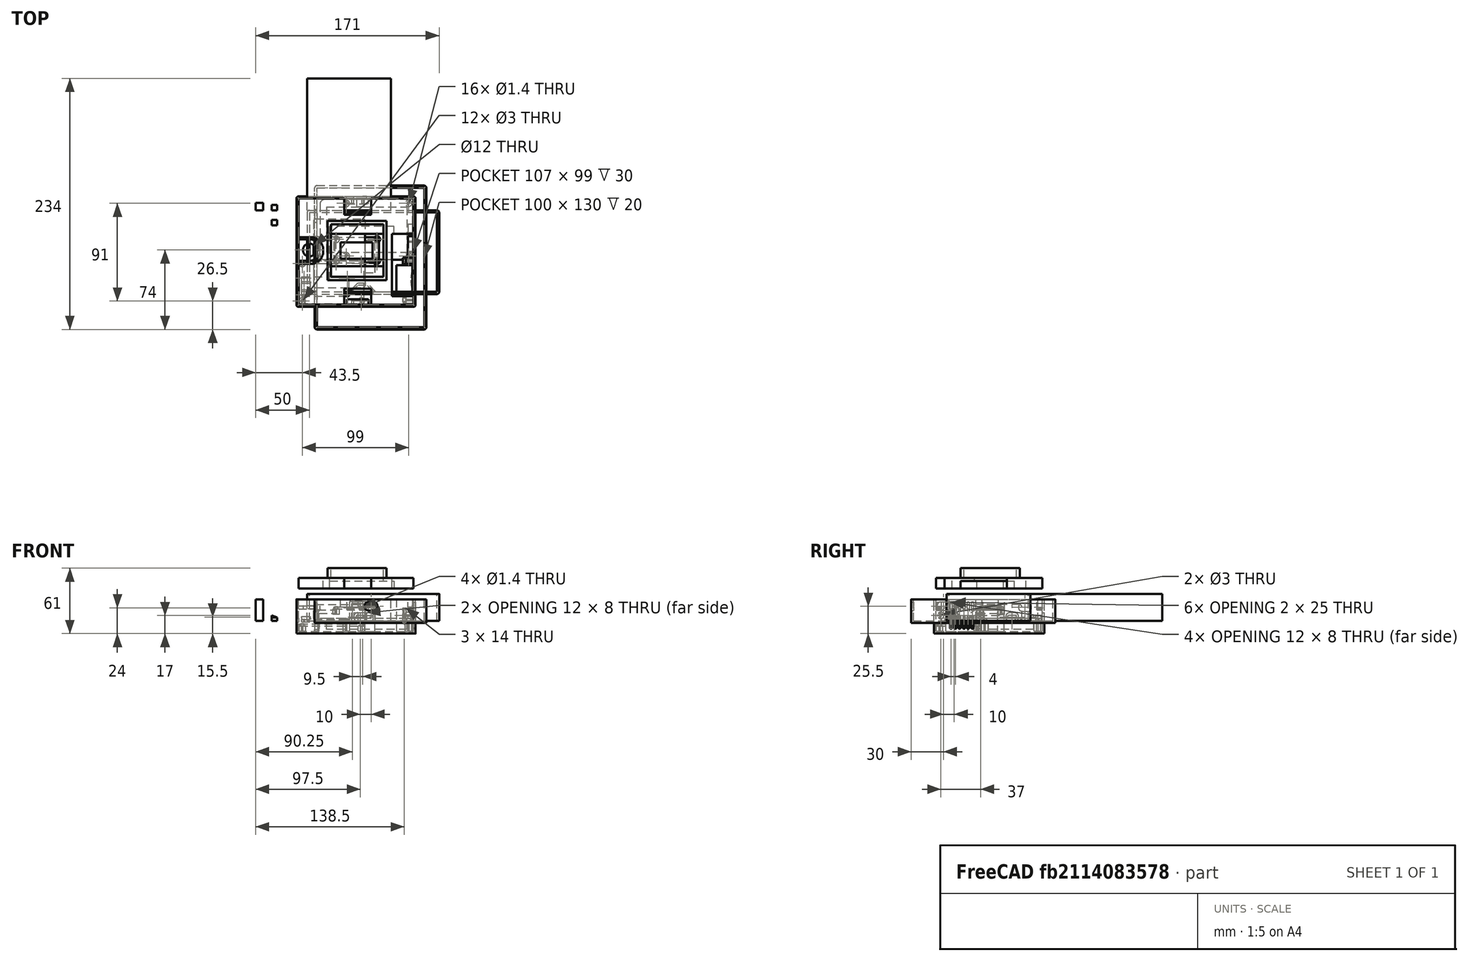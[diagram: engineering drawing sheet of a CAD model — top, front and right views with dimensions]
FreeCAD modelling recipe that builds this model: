
FCSTD DOCUMENT  (FreeCAD 1.0R39109 (Git))
Label: kitchen_timer
License: All rights reserved
LicenseURL: http://en.wikipedia.org/wiki/All_rights_reserved
objects: Part::Box×55, Part::Cut×34, Part::Cylinder×27, Part::Fillet×23, Part::MultiFuse×21, Part::FeaturePython×14, Part::Chamfer×4, Part::Sphere×1
note: 179 computed .brp shape members not serialized (recipe doc carries the construction recipe); baked Part::Feature solids carry a one-line shape summary decoded from their .brp

FEATURE [Part::Box] Box  label="Cube"
  AttacherType = Attacher::AttachEngine3D
  Height = 25
  Length = 78
  Width = 123
FEATURE [Part::Box] Box001  label="Cube001"
  AttacherType = Attacher::AttachEngine3D
  Height = 15
  Length = 64
  Placement = pos=(6,-8,0) rot=(0,0,1;-1.5708rad)
  Width = 48
FEATURE [Part::Box] Box002  label="Cube002"
  AttacherType = Attacher::AttachEngine3D
  Height = 25
  Length = 74
  Placement = pos=(2,2,0) rot=(0,0,1;0rad)
  Width = 119
FEATURE [Part::Box] Box003  label="Cube003"
  AttacherType = Attacher::AttachEngine3D
  Height = 25
  Length = 78
  Width = 123
FEATURE [Part::Fillet] Fillet
  Base = -> Box
  EdgeLinks = -> Box [Edge1,Edge3,Edge5]
  Edges = 3 edges r=2: [Edge1,Edge3,Edge5]
FEATURE [Part::Cut] Cut  label="case"
  Base = -> Fillet
  Placement = pos=(0,0,0) rot=(0,0,1;-1.5708rad)
  Tool = -> Box002
FEATURE [Part::Fillet] Fillet001  label="Battery pack_1"
  Base = -> Box001
  EdgeLinks = -> Box001 [Edge1,Edge2,Edge3,Edge4,Edge5,Edge6,Edge7,Edge8,Edge9,Edge10,Edge11,Edge12]
  Edges = 12 edges r=2: [Edge1,Edge2,Edge3,Edge4,Edge5,Edge6,Edge7,Edge8,Edge9,Edge10,Edge11,Edge12]
FEATURE [Part::Box] Box004  label="Cube004"
  AttacherType = Attacher::AttachEngine3D
  Height = 7
  Length = 30
  Placement = pos=(0,0,2) rot=(0,0,1;0rad)
  Width = 15
FEATURE [Part::Box] Box005  label="Cube005"
  AttacherType = Attacher::AttachEngine3D
  Height = 2
  Length = 42
  Placement = pos=(-6,-4,0) rot=(0,0,1;0rad)
  Width = 24
FEATURE [Part::MultiFuse] Fusion
  Shapes = -> [Box004,Box005]
FEATURE [Part::Cylinder] Cylinder
  Angle = 360
  AttacherType = Attacher::AttachEngine3D
  FirstAngle = 0
  Height = 10
  Placement = pos=(0,0,-2) rot=(0,0,1;0rad)
  Radius = 1.5
  SecondAngle = 0
FEATURE [Part::Cylinder] Cylinder001
  Angle = 360
  AttacherType = Attacher::AttachEngine3D
  FirstAngle = 0
  Height = 10
  Placement = pos=(38,0,-2) rot=(0,0,1;0rad)
  Radius = 1.5
  SecondAngle = 0
FEATURE [Part::Cylinder] Cylinder002
  Angle = 360
  AttacherType = Attacher::AttachEngine3D
  FirstAngle = 0
  Height = 10
  Placement = pos=(38,20,-2) rot=(0,0,1;0rad)
  Radius = 1.5
  SecondAngle = 0
FEATURE [Part::Cylinder] Cylinder003
  Angle = 360
  AttacherType = Attacher::AttachEngine3D
  FirstAngle = 0
  Height = 10
  Placement = pos=(0,20,-2) rot=(0,0,1;0rad)
  Radius = 1.5
  SecondAngle = 0
FEATURE [Part::MultiFuse] Fusion001
  Placement = pos=(-4,-2,0) rot=(0,0,1;0rad)
  Shapes = -> [Cylinder003,Cylinder,Cylinder001,Cylinder002]
FEATURE [Part::Cut] Cut001  label="display"
  Base = -> Fusion
  Placement = pos=(31,-45,11) rot=(0,0,1;0rad)
  Tool = -> Fusion001
FEATURE [Part::Box] Box006  label="Cube006"
  AttacherType = Attacher::AttachEngine3D
  Height = 15
  Length = 30
  Width = 28
FEATURE [Part::Sphere] Sphere
  Angle1 = -90
  Angle2 = 90
  Angle3 = 360
  AttacherType = Attacher::AttachEngine3D
  Placement = pos=(15,14,43.5) rot=(0,0,1;0rad)
  Radius = 30
FEATURE [Part::Cut] Cut002
  Base = -> Box006
  Tool = -> Sphere
FEATURE [Part::Box] Box007  label="Cube007"
  AttacherType = Attacher::AttachEngine3D
  Height = 3
  Length = 14
  Placement = pos=(8,27,6) rot=(0,0,1;0rad)
  Width = 8
FEATURE [Part::Chamfer] Chamfer
  Base = -> Box007
  EdgeLinks = -> Box007 [Edge3,Edge7]
  Edges = 2 edges r=6: [Edge3,Edge7]
FEATURE [Part::Cylinder] Cylinder004
  Angle = 360
  AttacherType = Attacher::AttachEngine3D
  FirstAngle = 0
  Height = 10
  Placement = pos=(15,32.5,0) rot=(0,0,1;0rad)
  Radius = 1.5
  SecondAngle = 0
FEATURE [Part::Cut] Cut003
  Base = -> Chamfer
  Tool = -> Cylinder004
FEATURE [Part::Box] Box008  label="Cube008"
  AttacherType = Attacher::AttachEngine3D
  Height = 3
  Length = 14
  Placement = pos=(8,27,6) rot=(0,0,1;0rad)
  Width = 8
FEATURE [Part::Chamfer] Chamfer001
  Base = -> Box008
  EdgeLinks = -> Box008 [Edge3,Edge7]
  Edges = 2 edges r=6: [Edge3,Edge7]
FEATURE [Part::Cylinder] Cylinder005
  Angle = 360
  AttacherType = Attacher::AttachEngine3D
  FirstAngle = 0
  Height = 10
  Placement = pos=(15,32.5,0) rot=(0,0,1;0rad)
  Radius = 1.5
  SecondAngle = 0
FEATURE [Part::Cut] Cut004
  Base = -> Chamfer001
  Placement = pos=(30,28,0) rot=(0,0,1;3.14159rad)
  Tool = -> Cylinder005
FEATURE [Part::MultiFuse] Fusion002  label="speaker"
  Placement = pos=(83,-79,20) rot=(0,1,0;1.5708rad)
  Shapes = -> [Cut003,Cut002,Cut004]
FEATURE [Part::Fillet] Fillet002  label="case001"
  Base = -> Cut
  EdgeLinks = -> Cut [Edge28]
  Edges = 1 edges r=2: [Edge28]
FEATURE [Part::Box] Box009  label="Cube009"
  AttacherType = Attacher::AttachEngine3D
  Height = 2
  Length = 44
  Width = 18
FEATURE [Part::Box] Box010  label="Cube010"
  AttacherType = Attacher::AttachEngine3D
  Height = 3
  Length = 8
  Placement = pos=(0,0,2) rot=(0,0,1;0rad)
  Width = 9
FEATURE [Part::Fillet] Fillet003
  Base = -> Box010
  EdgeLinks = -> Box010 [Edge9,Edge10,Edge11,Edge12]
  Edges = 4 edges r=1.4: [Edge9,Edge10,Edge11,Edge12]
  Placement = pos=(0,4.5,0) rot=(0,0,1;0rad)
FEATURE [Part::MultiFuse] Fusion003  label="nano"
  Placement = pos=(17,-22,14) rot=(0,0,1;0rad)
  Shapes = -> [Fillet003,Box009]
FEATURE [Part::Box] Box011  label="Cube011"
  AttacherType = Attacher::AttachEngine3D
  Height = 2
  Length = 86
  Placement = pos=(0,0,10) rot=(0,0,1;0rad)
  Width = 56
FEATURE [Part::Box] Box012  label="Cube012"
  AttacherType = Attacher::AttachEngine3D
  Height = 10
  Length = 75
  Placement = pos=(5,7,2) rot=(0,0,1;0rad)
  Width = 42
FEATURE [Part::Cylinder] Cylinder006
  Angle = 360
  AttacherType = Attacher::AttachEngine3D
  FirstAngle = 0
  Height = 10
  Radius = 1.5
  SecondAngle = 0
FEATURE [Part::Cylinder] Cylinder007
  Angle = 360
  AttacherType = Attacher::AttachEngine3D
  FirstAngle = 0
  Height = 10
  Placement = pos=(58,0,0) rot=(0,0,1;0rad)
  Radius = 1.5
  SecondAngle = 0
FEATURE [Part::Cylinder] Cylinder008
  Angle = 360
  AttacherType = Attacher::AttachEngine3D
  FirstAngle = 0
  Height = 10
  Placement = pos=(0,49,0) rot=(0,0,1;0rad)
  Radius = 1.5
  SecondAngle = 0
FEATURE [Part::Cylinder] Cylinder009
  Angle = 360
  AttacherType = Attacher::AttachEngine3D
  FirstAngle = 0
  Height = 10
  Placement = pos=(58,49,0) rot=(0,0,1;0rad)
  Radius = 1.5
  SecondAngle = 0
FEATURE [Part::MultiFuse] Fusion004
  Placement = pos=(6.5,-63.5,4) rot=(0,0,1;0rad)
  Shapes = -> [Cylinder006,Cylinder007,Cylinder008,Cylinder009]
FEATURE [Part::MultiFuse] Fusion005
  Placement = pos=(0,-67,0) rot=(0,0,1;0rad)
  Shapes = -> [Box011,Box012]
FEATURE [Part::Box] Box013  label="Cube013"
  AttacherType = Attacher::AttachEngine3D
  Height = 3
  Length = 7
  Placement = pos=(45,-67,12) rot=(0,0,1;0rad)
  Width = 7
FEATURE [Part::MultiFuse] Fusion006
  Placement = pos=(3,0,0) rot=(0,0,1;0rad)
  Shapes = -> [Fusion005,Box013]
FEATURE [Part::Cut] Cut005
  Base = -> Fusion006
  Tool = -> Fusion004
FEATURE [Part::Fillet] Fillet004  label="power_pack"
  Base = -> Cut005
  EdgeLinks = -> Cut005 [Edge28,Edge29,Edge31,Edge32]
  Edges = 4 edges r=4: [Edge28,Edge29,Edge31,Edge32]
  Placement = pos=(8,-41,0) rot=(0,0,1;0rad)
FEATURE [Part::Box] Box014  label="Cube014"
  AttacherType = Attacher::AttachEngine3D
  Height = 18
  Length = 20
  Placement = pos=(41.5,-76.5,0) rot=(0,0,1;0rad)
  Width = 9
FEATURE [Part::Chamfer] Chamfer002
  Base = -> Box014
  EdgeLinks = -> Box014 [Edge3,Edge7]
  Edges = 2 edges r=6: [Edge3,Edge7]
  Placement = pos=(0,-2,-2) rot=(0,0,1;0rad)
FEATURE [Part::Box] Box015  label="Cube015"
  AttacherType = Attacher::AttachEngine3D
  Height = 18
  Length = 24
  Placement = pos=(39.5,-76.5,0) rot=(0,0,1;0rad)
  Width = 9
FEATURE [Part::Chamfer] Chamfer003
  Base = -> Box015
  EdgeLinks = -> Box015 [Edge3,Edge7]
  Edges = 2 edges r=8: [Edge3,Edge7]
FEATURE [Part::MultiFuse] Fusion007
  Shapes = -> [Fillet002,Chamfer003]
FEATURE [Part::Cut] Cut006
  Base = -> Fusion007
  Tool = -> Chamfer002
FEATURE [Part::Cylinder] Cylinder010
  Angle = 360
  AttacherType = Attacher::AttachEngine3D
  FirstAngle = 0
  Height = 10
  Radius = 0.7
  SecondAngle = 0
FEATURE [Part::Cylinder] Cylinder011
  Angle = 360
  AttacherType = Attacher::AttachEngine3D
  FirstAngle = 0
  Height = 10
  Placement = pos=(40.5,0,0) rot=(0,0,1;0rad)
  Radius = 0.7
  SecondAngle = 0
FEATURE [Part::Cylinder] Cylinder012
  Angle = 360
  AttacherType = Attacher::AttachEngine3D
  FirstAngle = 0
  Height = 10
  Placement = pos=(0,15.5,0) rot=(0,0,1;0rad)
  Radius = 0.7
  SecondAngle = 0
FEATURE [Part::Cylinder] Cylinder013
  Angle = 360
  AttacherType = Attacher::AttachEngine3D
  FirstAngle = 0
  Height = 10
  Placement = pos=(40.5,15.5,0) rot=(0,0,1;0rad)
  Radius = 0.7
  SecondAngle = 0
FEATURE [Part::MultiFuse] Fusion008
  Placement = pos=(19,-20.75,7) rot=(0,0,1;0rad)
  Shapes = -> [Cylinder010,Cylinder011,Cylinder012,Cylinder013]
FEATURE [Part::Cut] Cut007  label="nano001"
  Base = -> Fusion003
  Placement = pos=(-15,29,-7) rot=(0,0,1;0rad)
  Tool = -> Fusion008
FEATURE [Part::Box] Box016  label="Cube016"
  AttacherType = Attacher::AttachEngine3D
  Height = 3
  Length = 4
  Placement = pos=(11,-85,12) rot=(0,0,1;0rad)
  Width = 8
FEATURE [Part::MultiFuse] Fusion009  label="power_pack001"
  Placement = pos=(109,-98,-10) rot=(0,0,1;3.14159rad)
  Shapes = -> [Fillet004,Box016]
FEATURE [Part::Box] Box017  label="Cube017"
  AttacherType = Attacher::AttachEngine3D
  Height = 2
  Length = 60
  Placement = pos=(0,0,3) rot=(0,0,1;0rad)
  Width = 40
FEATURE [Part::Cylinder] Cylinder014
  Angle = 360
  AttacherType = Attacher::AttachEngine3D
  FirstAngle = 0
  Height = 10
  Radius = 1.5
  SecondAngle = 0
FEATURE [Part::Cylinder] Cylinder015
  Angle = 360
  AttacherType = Attacher::AttachEngine3D
  FirstAngle = 0
  Height = 10
  Placement = pos=(55,0,0) rot=(0,0,1;0rad)
  Radius = 1.5
  SecondAngle = 0
FEATURE [Part::Cylinder] Cylinder016
  Angle = 360
  AttacherType = Attacher::AttachEngine3D
  FirstAngle = 0
  Height = 10
  Placement = pos=(0,35,0) rot=(0,0,1;0rad)
  Radius = 1.5
  SecondAngle = 0
FEATURE [Part::Cylinder] Cylinder017
  Angle = 360
  AttacherType = Attacher::AttachEngine3D
  FirstAngle = 0
  Height = 10
  Placement = pos=(55,35,0) rot=(0,0,1;0rad)
  Radius = 1.5
  SecondAngle = 0
FEATURE [Part::MultiFuse] Fusion010
  Placement = pos=(2.5,2.5,0) rot=(0,0,1;0rad)
  Shapes = -> [Cylinder014,Cylinder015,Cylinder016,Cylinder017]
FEATURE [Part::Cut] Cut008  label="board_1"
  Base = -> Box017
  Tool = -> Fusion010
FEATURE [Part::MultiFuse] Fusion011  label="nano_and_board"
  Placement = pos=(-7,-87,-8) rot=(0,0,1;0rad)
  Shapes = -> [Cut007,Cut008]
FEATURE [Part::FeaturePython] Tube  # WARN: FeaturePython — macro-defined, semantics opaque (R4)
  AttacherType = Attacher::AttachEngine3D
  Height = 5
  InnerRadius = 0.7
  OuterRadius = 3
  Placement = pos=(12.5,-18.5,0) rot=(0,0,1;0rad)
FEATURE [Part::FeaturePython] Tube001  # WARN: FeaturePython — macro-defined, semantics opaque (R4)
  AttacherType = Attacher::AttachEngine3D
  Height = 5
  InnerRadius = 0.7
  OuterRadius = 3
  Placement = pos=(67.5,-18.5,0) rot=(0,0,1;0rad)
FEATURE [Part::FeaturePython] Tube002  # WARN: FeaturePython — macro-defined, semantics opaque (R4)
  AttacherType = Attacher::AttachEngine3D
  Height = 5
  InnerRadius = 0.7
  OuterRadius = 3
  Placement = pos=(12.5,16.5,0) rot=(0,0,1;0rad)
FEATURE [Part::FeaturePython] Tube003  # WARN: FeaturePython — macro-defined, semantics opaque (R4)
  AttacherType = Attacher::AttachEngine3D
  Height = 5
  InnerRadius = 0.7
  OuterRadius = 3
  Placement = pos=(67.5,16.5,0) rot=(0,0,1;0rad)
FEATURE [Part::FeaturePython] Tube004  # WARN: FeaturePython — macro-defined, semantics opaque (R4)
  AttacherType = Attacher::AttachEngine3D
  Height = 7
  InnerRadius = 0.7
  OuterRadius = 3
  Placement = pos=(92,-9.5,0) rot=(0,0,1;0rad)
FEATURE [Part::FeaturePython] Tube005  # WARN: FeaturePython — macro-defined, semantics opaque (R4)
  AttacherType = Attacher::AttachEngine3D
  Height = 7
  InnerRadius = 0.7
  OuterRadius = 3
  Placement = pos=(92,-46.5,0) rot=(0,0,1;0rad)
FEATURE [Part::FeaturePython] Tube006  # WARN: FeaturePython — macro-defined, semantics opaque (R4)
  AttacherType = Attacher::AttachEngine3D
  Height = 5
  InnerRadius = 0.7
  OuterRadius = 3
  Placement = pos=(65,-47,0) rot=(0,0,1;0rad)
FEATURE [Part::FeaturePython] Tube007  # WARN: FeaturePython — macro-defined, semantics opaque (R4)
  AttacherType = Attacher::AttachEngine3D
  Height = 5
  InnerRadius = 0.7
  OuterRadius = 3
  Placement = pos=(65,-27,0) rot=(0,0,1;0rad)
FEATURE [Part::FeaturePython] Tube008  # WARN: FeaturePython — macro-defined, semantics opaque (R4)
  AttacherType = Attacher::AttachEngine3D
  Height = 5
  InnerRadius = 0.7
  OuterRadius = 3
  Placement = pos=(27,-27,0) rot=(0,0,1;0rad)
FEATURE [Part::FeaturePython] Tube009  # WARN: FeaturePython — macro-defined, semantics opaque (R4)
  AttacherType = Attacher::AttachEngine3D
  Height = 10
  InnerRadius = 0.7
  OuterRadius = 3
  Placement = pos=(14.5,-104.5,0) rot=(0,0,1;0rad)
FEATURE [Part::FeaturePython] Tube010  # WARN: FeaturePython — macro-defined, semantics opaque (R4)
  AttacherType = Attacher::AttachEngine3D
  Height = 5
  InnerRadius = 0.7
  OuterRadius = 3
  Placement = pos=(27,-47,0) rot=(0,0,1;0rad)
FEATURE [Part::FeaturePython] Tube011  # WARN: FeaturePython — macro-defined, semantics opaque (R4)
  AttacherType = Attacher::AttachEngine3D
  Height = 10
  InnerRadius = 0.7
  OuterRadius = 3
  Placement = pos=(14.5,-55.5,0) rot=(0,0,1;0rad)
FEATURE [Part::FeaturePython] Tube012  # WARN: FeaturePython — macro-defined, semantics opaque (R4)
  AttacherType = Attacher::AttachEngine3D
  Height = 10
  InnerRadius = 0.7
  OuterRadius = 3
  Placement = pos=(72.5,-55.5,0) rot=(0,0,1;0rad)
FEATURE [Part::FeaturePython] Tube013  # WARN: FeaturePython — macro-defined, semantics opaque (R4)
  AttacherType = Attacher::AttachEngine3D
  Height = 10
  InnerRadius = 0.7
  OuterRadius = 3
  Placement = pos=(72.5,-104.5,0) rot=(0,0,1;0rad)
FEATURE [Part::Box] Box018  label="Cube018"
  AttacherType = Attacher::AttachEngine3D
  Height = 20
  Length = 100
  Placement = pos=(9,-109,0) rot=(0,0,1;0rad)
  Width = 130
FEATURE [Part::Box] Box019  label="Cube019"
  AttacherType = Attacher::AttachEngine3D
  Height = 22
  Length = 104
  Placement = pos=(7,-111,-2) rot=(0,0,1;0rad)
  Width = 134
FEATURE [Part::Cut] Cut009
  Base = -> Box019
  Tool = -> Box018
FEATURE [Part::Box] Box020  label="Cube020"
  AttacherType = Attacher::AttachEngine3D
  Height = 8
  Length = 10
  Placement = pos=(4,-3,0) rot=(0,0,1;0rad)
  Width = 12
FEATURE [Part::Fillet] Fillet005
  Base = -> Box020
  EdgeLinks = -> Box020 [Edge9,Edge10,Edge11,Edge12]
  Edges = 4 edges r=3.7: [Edge9,Edge10,Edge11,Edge12]
  Placement = pos=(0,-8,8.5) rot=(0,0,1;0rad)
FEATURE [Part::Box] Box021  label="Cube021"
  AttacherType = Attacher::AttachEngine3D
  Height = 8
  Length = 10
  Placement = pos=(4,-3,0) rot=(0,0,1;0rad)
  Width = 12
FEATURE [Part::Fillet] Fillet006
  Base = -> Box021
  EdgeLinks = -> Box021 [Edge9,Edge10,Edge11,Edge12]
  Edges = 4 edges r=3.7: [Edge9,Edge10,Edge11,Edge12]
  Placement = pos=(0,-84,9.5) rot=(0,0,1;0rad)
FEATURE [Part::Box] Box022  label="Cube022"
  AttacherType = Attacher::AttachEngine3D
  Height = 8
  Length = 10
  Placement = pos=(4,-3,0) rot=(0,0,1;0rad)
  Width = 12
FEATURE [Part::Fillet] Fillet007
  Base = -> Box022
  EdgeLinks = -> Box022 [Edge9,Edge10,Edge11,Edge12]
  Edges = 4 edges r=3.7: [Edge9,Edge10,Edge11,Edge12]
  Placement = pos=(62.5,-118,9.5) rot=(0,0,1;1.5708rad)
FEATURE [Part::Cut] Cut010
  Base = -> Cut009
  Tool = -> Fillet005
FEATURE [Part::Cut] Cut011
  Base = -> Cut010
  Tool = -> Fillet007
FEATURE [Part::Cut] Cut012
  Base = -> Cut011
  Tool = -> Fillet006
FEATURE [Part::Fillet] Fillet008
  Base = -> Cut012
  EdgeLinks = -> Cut012 [Edge1,Edge4,Edge22,Edge40]
  Edges = 4 edges r=2: [Edge1,Edge4,Edge22,Edge40]
FEATURE [Part::Box] Box023  label="Cube023"
  AttacherType = Attacher::AttachEngine3D
  Height = 10
  Length = 20
  Placement = pos=(57,16,10) rot=(0,0,1;0rad)
  Width = 5
FEATURE [Part::Cylinder] Cylinder018
  Angle = 360
  AttacherType = Attacher::AttachEngine3D
  FirstAngle = 0
  Height = 10
  Placement = pos=(71.75,22,17) rot=(1,0,0;1.5708rad)
  Radius = 0.7
  SecondAngle = 0
FEATURE [Part::Cylinder] Cylinder019
  Angle = 360
  AttacherType = Attacher::AttachEngine3D
  FirstAngle = 0
  Height = 10
  Placement = pos=(62.25,22,17) rot=(1,0,0;1.5708rad)
  Radius = 0.7
  SecondAngle = 0
FEATURE [Part::MultiFuse] Fusion013
  Placement = pos=(0,0,-5) rot=(0,0,1;0rad)
  Shapes = -> [Cylinder019,Cylinder018]
FEATURE [Part::Cut] Cut013  label="up_button_stand"
  Base = -> Box023
  Placement = pos=(-20,-10,0) rot=(0,0,1;0rad)
  Tool = -> Fusion013
FEATURE [Part::Box] Box024  label="Cube024"
  AttacherType = Attacher::AttachEngine3D
  Height = 10
  Length = 20
  Placement = pos=(57,16,10) rot=(0,0,1;0rad)
  Width = 5
FEATURE [Part::Cylinder] Cylinder020
  Angle = 360
  AttacherType = Attacher::AttachEngine3D
  FirstAngle = 0
  Height = 10
  Placement = pos=(71.75,22,17) rot=(1,0,0;1.5708rad)
  Radius = 0.7
  SecondAngle = 0
FEATURE [Part::Cylinder] Cylinder021
  Angle = 360
  AttacherType = Attacher::AttachEngine3D
  FirstAngle = 0
  Height = 10
  Placement = pos=(62.25,22,17) rot=(1,0,0;1.5708rad)
  Radius = 0.7
  SecondAngle = 0
FEATURE [Part::MultiFuse] Fusion014
  Placement = pos=(0,0,-5) rot=(0,0,1;0rad)
  Shapes = -> [Cylinder021,Cylinder020]
FEATURE [Part::Cut] Cut014  label="down_button_stand"
  Base = -> Box024
  Placement = pos=(-20,-104,0) rot=(0,0,1;0rad)
  Tool = -> Fusion014
FEATURE [Part::MultiFuse] Fusion015  label="boardstand"
  Placement = pos=(-17,-66,-10) rot=(0,0,1;0rad)
  Shapes = -> [Tube,Tube001,Tube002,Tube003]
FEATURE [Part::MultiFuse] Fusion016  label="spkrstand"
  Placement = pos=(92,-37,97) rot=(0,1,0;1.5708rad)
  Shapes = -> [Tube004,Tube005]
FEATURE [Part::MultiFuse] Fusion017  label="dsplystand"
  Placement = pos=(0,0,6) rot=(0,0,1;0rad)
  Shapes = -> [Tube006,Tube007,Tube008,Tube010]
FEATURE [Part::MultiFuse] Fusion018  label="powerstand"
  Placement = pos=(22,62,-10) rot=(0,0,1;0rad)
  Shapes = -> [Tube009,Tube011,Tube012,Tube013]
FEATURE [Part::Box] Box025  label="Cube025"
  AttacherType = Attacher::AttachEngine3D
  Height = 10
  Length = 20
  Placement = pos=(57,16,10) rot=(0,0,1;0rad)
  Width = 5
FEATURE [Part::Cylinder] Cylinder022
  Angle = 360
  AttacherType = Attacher::AttachEngine3D
  FirstAngle = 0
  Height = 10
  Placement = pos=(71.75,22,17) rot=(1,0,0;1.5708rad)
  Radius = 0.7
  SecondAngle = 0
FEATURE [Part::Cylinder] Cylinder023
  Angle = 360
  AttacherType = Attacher::AttachEngine3D
  FirstAngle = 0
  Height = 10
  Placement = pos=(62.25,22,17) rot=(1,0,0;1.5708rad)
  Radius = 0.7
  SecondAngle = 0
FEATURE [Part::MultiFuse] Fusion019
  Placement = pos=(0,0,-5) rot=(0,0,1;0rad)
  Shapes = -> [Cylinder023,Cylinder022]
FEATURE [Part::Cut] Cut015  label="right_button_stand"
  Base = -> Box025
  Placement = pos=(115,-101,0) rot=(0,0,1;1.5708rad)
  Tool = -> Fusion019
FEATURE [Part::Box] Box026  label="Cube026"
  AttacherType = Attacher::AttachEngine3D
  Height = 3
  Length = 20
  Placement = pos=(-10,-10,4) rot=(0,0,1;0rad)
  Width = 20
FEATURE [Part::Cylinder] Cylinder024
  Angle = 360
  AttacherType = Attacher::AttachEngine3D
  FirstAngle = 0
  Height = 10
  Radius = 6
  SecondAngle = 0
FEATURE [Part::Cut] Cut016
  Base = -> Box026
  Placement = pos=(2,-37,7) rot=(0,0,1;0rad)
  Tool = -> Cylinder024
FEATURE [Part::Box] Box027  label="Cube027"
  AttacherType = Attacher::AttachEngine3D
  Height = 32
  Length = 107
  Placement = pos=(-8,-88,-10) rot=(0,0,1;0rad)
  Width = 99
FEATURE [Part::Box] Box028  label="Cube028"
  AttacherType = Attacher::AttachEngine3D
  Height = 32
  Length = 111
  Placement = pos=(-10,-90,-12) rot=(0,0,1;0rad)
  Width = 103
FEATURE [Part::Cut] Cut017
  Base = -> Box028
  Tool = -> Box027
FEATURE [Part::Fillet] Fillet009
  Base = -> Cut016
  EdgeLinks = -> Cut016 [Edge6,Edge12]
  Edges = 2 edges r=9.7: [Edge6,Edge12]
FEATURE [Part::Box] Box029  label="Cube029"
  AttacherType = Attacher::AttachEngine3D
  Height = 20
  Length = 19
  Placement = pos=(7,0,-10) rot=(0,0,1;0rad)
  Width = 25
FEATURE [Part::Box] Box030  label="Cube030"
  AttacherType = Attacher::AttachEngine3D
  Height = 20
  Length = 19
  Placement = pos=(11,0,-13) rot=(0,0,1;0rad)
  Width = 25
FEATURE [Part::Cut] Cut018
  Base = -> Box029
  Placement = pos=(0,-49.5,0) rot=(0,0,1;0rad)
  Tool = -> Box030
FEATURE [Part::Cylinder] Cylinder025
  Angle = 360
  AttacherType = Attacher::AttachEngine3D
  FirstAngle = 0
  Height = 30
  Placement = pos=(2,-37,-13) rot=(0,0,1;0rad)
  Radius = 8
  SecondAngle = 0
FEATURE [Part::Cut] Cut019
  Base = -> Cut018
  Tool = -> Cylinder025
FEATURE [Part::Cylinder] Cylinder026
  Angle = 360
  AttacherType = Attacher::AttachEngine3D
  FirstAngle = 0
  Height = 10
  Placement = pos=(2,-49.5,-4) rot=(0,1,0;1.5708rad)
  Radius = 4
  SecondAngle = 0
FEATURE [Part::Cut] Cut020
  Base = -> Cut019
  Tool = -> Cylinder026
FEATURE [Part::Box] Box031  label="Cube031"
  AttacherType = Attacher::AttachEngine3D
  Height = 20
  Length = 9
  Placement = pos=(54,-58,-10) rot=(0,0,1;0rad)
  Width = 30
FEATURE [Part::Box] Box032  label="Cube032"
  AttacherType = Attacher::AttachEngine3D
  Height = 15
  Length = 9
  Placement = pos=(54,-48,-10) rot=(0,0,1;0rad)
  Width = 20
FEATURE [Part::Cut] Cut021
  Base = -> Box031
  Tool = -> Box032
FEATURE [Part::Fillet] Fillet010
  Base = -> Cut021
  EdgeLinks = -> Cut021 [Edge9]
  Edges = 1 edges r=9: [Edge9]
FEATURE [Part::Fillet] Fillet011
  Base = -> Cut020
  EdgeLinks = -> Cut020 [Edge1,Edge7,Edge8,Edge9]
  Edges = 4 edges r=3: [Edge1,Edge7,Edge8,Edge9]
FEATURE [Part::Fillet] Fillet012
  Base = -> Cut017
  EdgeLinks = -> Cut017 [Edge1,Edge3,Edge6,Edge15]
  Edges = 4 edges r=2: [Edge1,Edge3,Edge6,Edge15]
FEATURE [Part::Box] Box033  label="Cube033"
  AttacherType = Attacher::AttachEngine3D
  Height = 2
  Length = 10
  Placement = pos=(95,-77.5,-7) rot=(0,0,1;0rad)
  Width = 25
FEATURE [Part::Fillet] Fillet013
  Base = -> Box033
  EdgeLinks = -> Box033 [Edge1,Edge2,Edge3,Edge4,Edge5,Edge6,Edge7,Edge8,Edge9,Edge10,Edge11,Edge12]
  Edges = 12 edges r=0.8: [Edge1,Edge2,Edge3,Edge4,Edge5,Edge6,Edge7,Edge8,Edge9,Edge10,Edge11,Edge12]
  Placement = pos=(1,-60,70) rot=(1,0,0;1.5708rad)
FEATURE [Part::Box] Box034  label="Cube034"
  AttacherType = Attacher::AttachEngine3D
  Height = 2
  Length = 10
  Placement = pos=(95,-77.5,-7) rot=(0,0,1;0rad)
  Width = 25
FEATURE [Part::Fillet] Fillet014
  Base = -> Box034
  EdgeLinks = -> Box034 [Edge1,Edge2,Edge3,Edge4,Edge5,Edge6,Edge7,Edge8,Edge9,Edge10,Edge11,Edge12]
  Edges = 12 edges r=0.8: [Edge1,Edge2,Edge3,Edge4,Edge5,Edge6,Edge7,Edge8,Edge9,Edge10,Edge11,Edge12]
  Placement = pos=(1,-64,70) rot=(1,0,0;1.5708rad)
FEATURE [Part::Box] Box035  label="Cube035"
  AttacherType = Attacher::AttachEngine3D
  Height = 2
  Length = 10
  Placement = pos=(95,-77.5,-7) rot=(0,0,1;0rad)
  Width = 25
FEATURE [Part::Fillet] Fillet015
  Base = -> Box035
  EdgeLinks = -> Box035 [Edge1,Edge2,Edge3,Edge4,Edge5,Edge6,Edge7,Edge8,Edge9,Edge10,Edge11,Edge12]
  Edges = 12 edges r=0.8: [Edge1,Edge2,Edge3,Edge4,Edge5,Edge6,Edge7,Edge8,Edge9,Edge10,Edge11,Edge12]
  Placement = pos=(1,-68,70) rot=(1,0,0;1.5708rad)
FEATURE [Part::Box] Box036  label="Cube036"
  AttacherType = Attacher::AttachEngine3D
  Height = 2
  Length = 10
  Placement = pos=(95,-77.5,-7) rot=(0,0,1;0rad)
  Width = 25
FEATURE [Part::Fillet] Fillet016
  Base = -> Box036
  EdgeLinks = -> Box036 [Edge1,Edge2,Edge3,Edge4,Edge5,Edge6,Edge7,Edge8,Edge9,Edge10,Edge11,Edge12]
  Edges = 12 edges r=0.8: [Edge1,Edge2,Edge3,Edge4,Edge5,Edge6,Edge7,Edge8,Edge9,Edge10,Edge11,Edge12]
  Placement = pos=(1,-72,70) rot=(1,0,0;1.5708rad)
FEATURE [Part::Box] Box037  label="Cube037"
  AttacherType = Attacher::AttachEngine3D
  Height = 2
  Length = 10
  Placement = pos=(95,-77.5,-7) rot=(0,0,1;0rad)
  Width = 25
FEATURE [Part::Fillet] Fillet017
  Base = -> Box037
  EdgeLinks = -> Box037 [Edge1,Edge2,Edge3,Edge4,Edge5,Edge6,Edge7,Edge8,Edge9,Edge10,Edge11,Edge12]
  Edges = 12 edges r=0.8: [Edge1,Edge2,Edge3,Edge4,Edge5,Edge6,Edge7,Edge8,Edge9,Edge10,Edge11,Edge12]
  Placement = pos=(1,-76,70) rot=(1,0,0;1.5708rad)
FEATURE [Part::Box] Box038  label="Cube038"
  AttacherType = Attacher::AttachEngine3D
  Height = 2
  Length = 10
  Placement = pos=(95,-77.5,-7) rot=(0,0,1;0rad)
  Width = 25
FEATURE [Part::Fillet] Fillet018
  Base = -> Box038
  EdgeLinks = -> Box038 [Edge1,Edge2,Edge3,Edge4,Edge5,Edge6,Edge7,Edge8,Edge9,Edge10,Edge11,Edge12]
  Edges = 12 edges r=0.8: [Edge1,Edge2,Edge3,Edge4,Edge5,Edge6,Edge7,Edge8,Edge9,Edge10,Edge11,Edge12]
  Placement = pos=(1,-80,70) rot=(1,0,0;1.5708rad)
FEATURE [Part::MultiFuse] Fusion020
  Shapes = -> [Fillet018,Fillet013,Fillet014,Fillet015,Fillet016,Fillet017]
FEATURE [Part::Cut] Cut022
  Base = -> Fillet012
  Tool = -> Fusion020
FEATURE [Part::Box] Box039  label="Cube039"
  AttacherType = Attacher::AttachEngine3D
  Height = 8
  Length = 12
  Width = 12
FEATURE [Part::Fillet] Fillet019
  Base = -> Box039
  EdgeLinks = -> Box039 [Edge1,Edge2,Edge3,Edge4,Edge5,Edge6,Edge7,Edge8,Edge9,Edge10,Edge11,Edge12]
  Edges = 12 edges r=3.8: [Edge1,Edge2,Edge3,Edge4,Edge5,Edge6,Edge7,Edge8,Edge9,Edge10,Edge11,Edge12]
  Placement = pos=(43.5,6,-0.5) rot=(0,0,1;0rad)
FEATURE [Part::Box] Box040  label="Cube040"
  AttacherType = Attacher::AttachEngine3D
  Height = 8
  Length = 12
  Width = 12
FEATURE [Part::Fillet] Fillet020
  Base = -> Box040
  EdgeLinks = -> Box040 [Edge1,Edge2,Edge3,Edge4,Edge5,Edge6,Edge7,Edge8,Edge9,Edge10,Edge11,Edge12]
  Edges = 12 edges r=3.8: [Edge1,Edge2,Edge3,Edge4,Edge5,Edge6,Edge7,Edge8,Edge9,Edge10,Edge11,Edge12]
  Placement = pos=(-15,-77,-1.5) rot=(0,0,1;0rad)
FEATURE [Part::Box] Box041  label="Cube041"
  AttacherType = Attacher::AttachEngine3D
  Height = 8
  Length = 12
  Width = 12
FEATURE [Part::Fillet] Fillet021
  Base = -> Box041
  EdgeLinks = -> Box041 [Edge1,Edge2,Edge3,Edge4,Edge5,Edge6,Edge7,Edge8,Edge9,Edge10,Edge11,Edge12]
  Edges = 12 edges r=3.8: [Edge1,Edge2,Edge3,Edge4,Edge5,Edge6,Edge7,Edge8,Edge9,Edge10,Edge11,Edge12]
  Placement = pos=(94,-23,-0.5) rot=(0,0,1;0rad)
FEATURE [Part::Cut] Cut023
  Base = -> Cut022
  Tool = -> Fillet021
FEATURE [Part::Cut] Cut024
  Base = -> Cut023
  Tool = -> Fillet019
FEATURE [Part::Cut] Cut025
  Base = -> Cut024
  Tool = -> Fillet020
FEATURE [Part::Box] Box042  label="Cube042"
  AttacherType = Attacher::AttachEngine3D
  Height = 10
  Length = 10
  Placement = pos=(-36,0,6) rot=(0,1,0;0.349066rad)
  Width = 7
FEATURE [Part::Box] Box043  label="Cube043"
  AttacherType = Attacher::AttachEngine3D
  Height = 3
  Length = 5
  Placement = pos=(-33,-14,0) rot=(0,0,1;0rad)
  Width = 5
FEATURE [Part::Box] Box044  label="Cube044"
  AttacherType = Attacher::AttachEngine3D
  Height = 5
  Length = 5
  Placement = pos=(-33,0,0) rot=(0,0,1;0rad)
  Width = 5
FEATURE [Part::Cut] Cut026
  Base = -> Box044
  Tool = -> Box042
FEATURE [Part::Box] Box045  label="Cube045"
  AttacherType = Attacher::AttachEngine3D
  Height = 20
  Length = 7
  Placement = pos=(-48,0,0) rot=(0,0,1;0rad)
  Width = 7
FEATURE [Part::Box] Box046  label="Cube046"
  AttacherType = Attacher::AttachEngine3D
  Height = 10
  Length = 107
  Placement = pos=(-8,-88,30) rot=(0,0,1;0rad)
  Width = 99
FEATURE [Part::Box] Box047  label="Cube047"
  AttacherType = Attacher::AttachEngine3D
  Height = 10
  Length = 50
  Placement = pos=(21,-52,30) rot=(0,0,1;0rad)
  Width = 30
FEATURE [Part::Cut] Cut027
  Base = -> Box046
  Tool = -> Box047
FEATURE [Part::Box] Box048  label="Cube048"
  AttacherType = Attacher::AttachEngine3D
  Height = 10
  Length = 25
  Placement = pos=(-8,-88,30) rot=(0,0,1;0rad)
  Width = 25
FEATURE [Part::Box] Box049  label="Cube049"
  AttacherType = Attacher::AttachEngine3D
  Height = 10
  Length = 25
  Placement = pos=(34.5,-93,30) rot=(0,0,1;0rad)
  Width = 20
FEATURE [Part::Fillet] Fillet022
  Base = -> Box048
  EdgeLinks = -> Box048 [Edge5,Edge7]
  Edges = 2 edges r=12: [Edge5,Edge7]
  Placement = pos=(-2,38,0) rot=(0,0,1;0rad)
FEATURE [Part::Cut] Cut028
  Base = -> Cut027
  Tool = -> Fillet022
FEATURE [Part::Box] Box050  label="Cube050"
  AttacherType = Attacher::AttachEngine3D
  Height = 10
  Length = 60
  Placement = pos=(21,-65,27) rot=(0,0,1;0rad)
  Width = 50
FEATURE [Part::Box] Box051  label="Cube051"
  AttacherType = Attacher::AttachEngine3D
  Height = 10
  Length = 25
  Placement = pos=(34.5,-4,30) rot=(0,0,1;0rad)
  Width = 20
FEATURE [Part::Box] Box052  label="Cube052"
  AttacherType = Attacher::AttachEngine3D
  Height = 10
  Length = 20
  Placement = pos=(79,-80,30) rot=(0,0,1;0rad)
  Width = 58
FEATURE [Part::Cut] Cut029
  Base = -> Cut028
  Tool = -> Box051
FEATURE [Part::Cut] Cut030
  Base = -> Cut029
  Tool = -> Box049
FEATURE [Part::Cut] Cut031
  Base = -> Cut030
  Tool = -> Box052
FEATURE [Part::Cut] Cut032
  Base = -> Cut031
  Tool = -> Box050
FEATURE [Part::Box] Box053  label="Cube053"
  AttacherType = Attacher::AttachEngine3D
  Height = 9
  Length = 55
  Placement = pos=(19,-65,39) rot=(0,0,1;0rad)
  Width = 55
FEATURE [Part::Box] Box054  label="Cube054"
  AttacherType = Attacher::AttachEngine3D
  Height = 9
  Length = 49
  Placement = pos=(22,-62,39) rot=(0,0,1;0rad)
  Width = 49
FEATURE [Part::Cut] Cut033
  Base = -> Box053
  Placement = pos=(0,0,1) rot=(0,0,1;0rad)
  Tool = -> Box054
FEATURE [Part::MultiFuse] Fusion021
  Shapes = -> [Cut033,Cut032]
